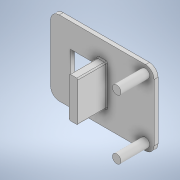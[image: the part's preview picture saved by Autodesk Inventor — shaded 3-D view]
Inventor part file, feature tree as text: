
AUTODESK INVENTOR PART (.ipt)
format: ipt  version: 2020 (Build 240168000, 168)  size: 157,184 bytes
history: native  units: mm
features: extrude x3, sketch x3, fillet x1
ambient origin geometry x8: Origin, YZ Plane, XZ Plane, XY Plane, X Axis, Y Axis, Z Axis, Center Point
bodies: Solid1 (feature_tree)
feature tree (7):
  extrude  "Extrusion1"  Depth=130.0mm
  extrude  "Extrusion2"  Depth=15.0mm
  extrude  "Extrusion3"  Depth=15.0mm
  fillet  "Fillet1"  Radius=104.0mm
  sketch  "Sketch1"  dims[d0=180.0mm d1=130.0mm]
  sketch  "Sketch3"  dims[d2=7.0mm d3=0.0mm d9=15.0mm]
  sketch  "Sketch4"  dims[d10=15.0mm d11=15.0mm d12=104.0mm d13=52.0mm d14=75.0mm d15=15.0mm d16=70.0mm d17=7.5mm d18=35.0mm d19=50.0mm d20=0.0mm d21=46.0mm d22=40.0mm d23=50.0mm d24=0.0mm d25=28.0mm d26=2.0mm]
